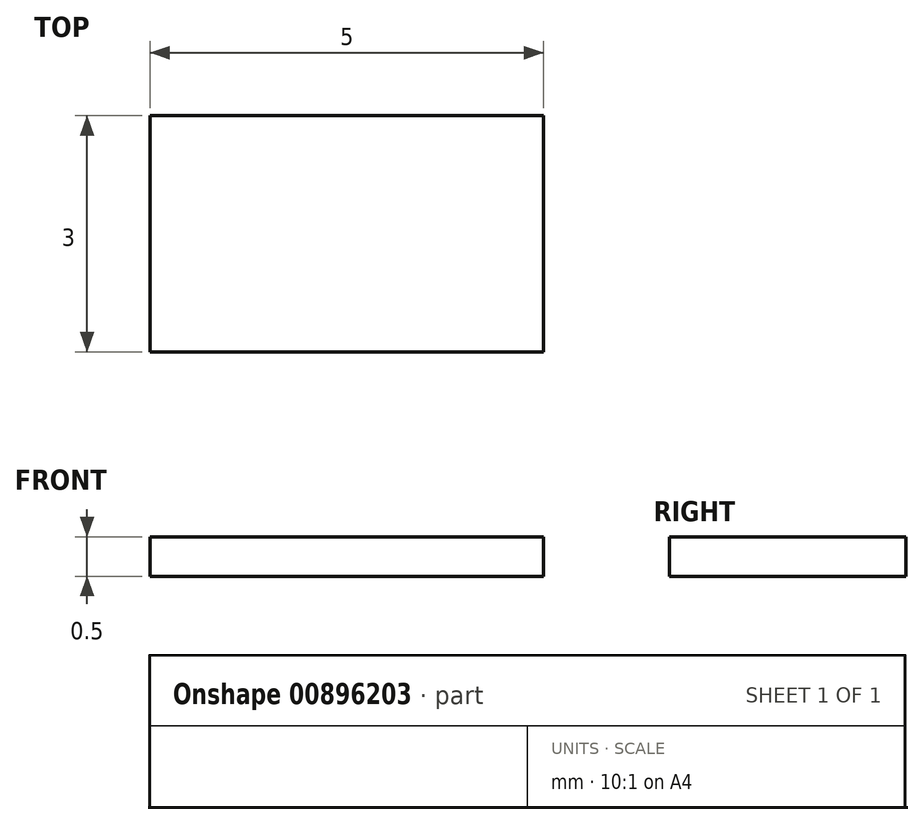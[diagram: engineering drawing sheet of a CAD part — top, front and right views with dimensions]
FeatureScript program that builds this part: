
annotation { "Feature Type Name" : "Feature", "Feature Type Description" : "" }
export const myFeature = defineFeature(function(context is Context, id is Id, definition is map)
    precondition{}
    {
        {
            var Q0;
            Q0=qCreatedBy(makeId("Top.planeOp"),FACE);
            var sketch = newSketch(context, id + "F0", { "sketchPlane" : qUnion([Q0])});
            skLineSegment(sketch, "E0.bottom", {"start": v(2.5, 1.5) * mm, "end": v(-2.5, 1.5) * mm});
            skLineSegment(sketch, "E0.top", {"start": v(2.5, -1.5) * mm, "end": v(-2.5, -1.5) * mm});
            skLineSegment(sketch, "E0.left", {"start": v(2.5, 1.5) * mm, "end": v(2.5, -1.5) * mm});
            skLineSegment(sketch, "E0.right", {"start": v(-2.5, 1.5) * mm, "end": v(-2.5, -1.5) * mm});
            skPoint(sketch, "E0.middle", {"position": v(0, 0) * mm});
            skSolve(sketch);
        }
        {
            var Q0;
            Q0=makeQuery(id+"F0.imprint","IMPRINT",FACE,{"disambiguationData":[TD([[makeQuery(id+"F0.imprint","IMPRINT",EDGE,{"derivedFrom":sQuery(id+"F0.wireOp",EDGE,"E0.bottom")}),1.0]])]});
            extrude(context, id + "F1", {"entities" : qUnion([Q0]), "depth" : 0.5 * mm, "offsetDistance" : 25 * mm});
        }
    });
